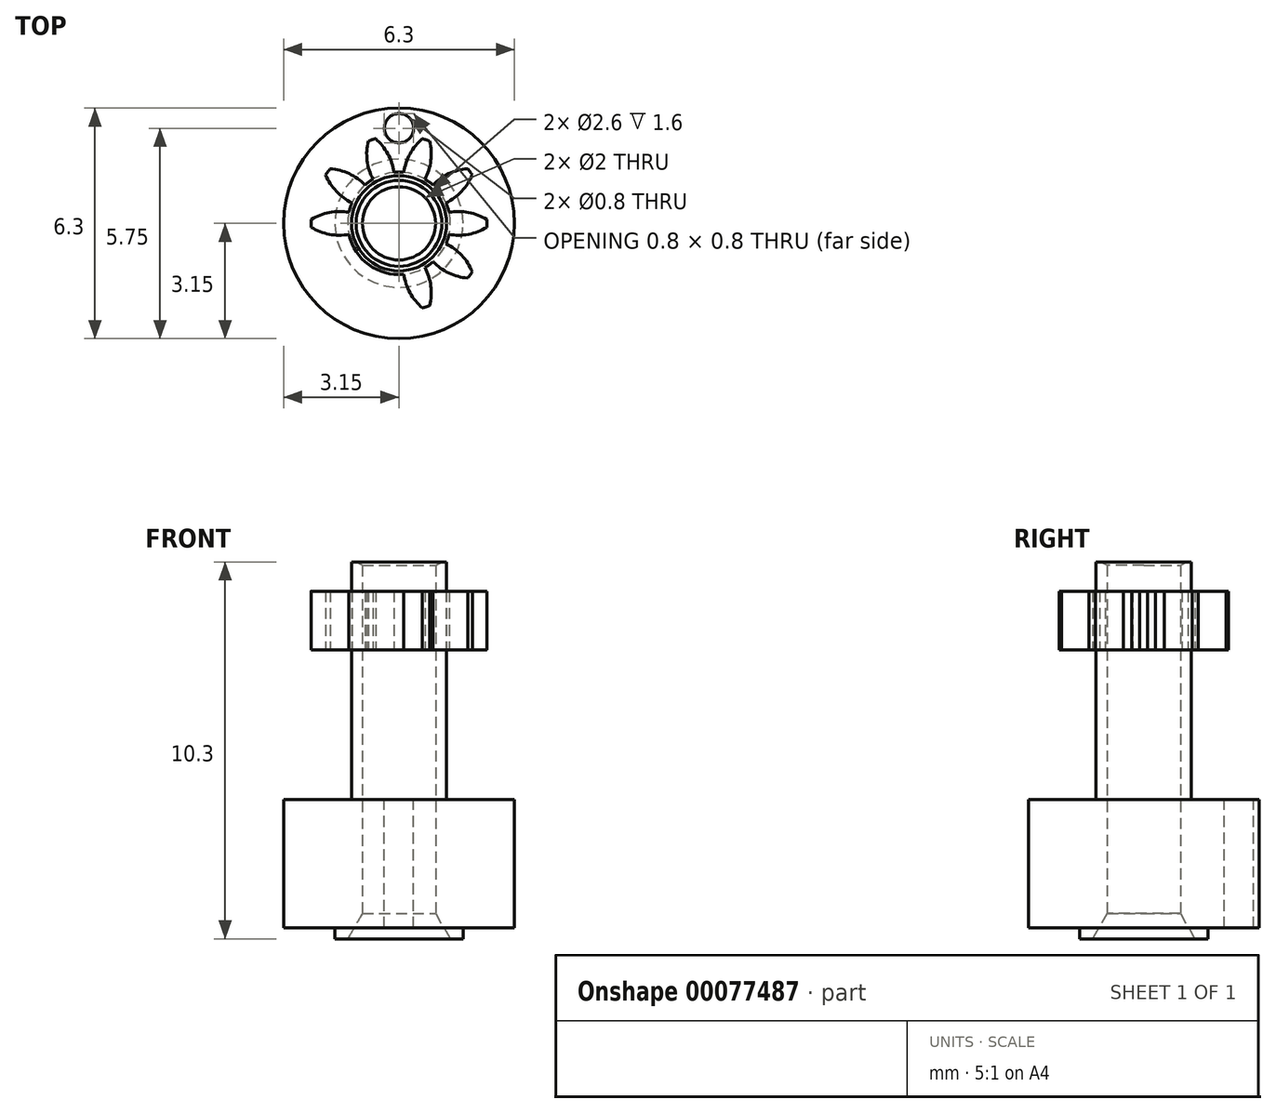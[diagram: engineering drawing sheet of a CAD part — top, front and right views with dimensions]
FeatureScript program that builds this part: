
annotation { "Feature Type Name" : "Feature", "Feature Type Description" : "" }
export const myFeature = defineFeature(function(context is Context, id is Id, definition is map)
    precondition{}
    {
        {
            var Q0;
            Q0=qCreatedBy(makeId("Front.planeOp"),FACE);
            var sketch = newSketch(context, id + "F0", { "sketchPlane" : qUnion([Q0])});
            skLineSegment(sketch, "E0", {"start": v(1.4, 0) * mm, "end": v(1.75, 0) * mm});
            skLineSegment(sketch, "E1", {"start": v(1.75, 0) * mm, "end": v(1.75, 0.3) * mm});
            skLineSegment(sketch, "E2", {"start": v(1.75, 0.3) * mm, "end": v(3.15, 0.3) * mm});
            skLineSegment(sketch, "E3", {"start": v(3.15, 0.3) * mm, "end": v(3.15, 3.8) * mm});
            skLineSegment(sketch, "E4", {"start": v(3.15, 3.8) * mm, "end": v(1.3, 3.8) * mm});
            skLineSegment(sketch, "E5", {"start": v(1.3, 3.8) * mm, "end": v(1.3, 10.3) * mm});
            skLineSegment(sketch, "E6", {"start": v(1.3, 10.3) * mm, "end": v(1, 10.3) * mm});
            skLineSegment(sketch, "E7", {"start": v(1, 10.3) * mm, "end": v(1, 0.7) * mm});
            skLineSegment(sketch, "E8", {"start": v(1, 0.7) * mm, "end": v(1.4, 0) * mm});
            skLineSegment(sketch, "E9", {"start": v(0, 0) * mm, "end": v(0, 10.3) * mm, "construction": true});
            skSolve(sketch);
        }
        {
            var Q0;
            Q0=makeQuery(id+"F0.imprint","IMPRINT",FACE,{"disambiguationData":[TD([[makeQuery(id+"F0.imprint","IMPRINT",EDGE,{"derivedFrom":sQuery(id+"F0.wireOp",EDGE,"E0")}),1.0]])]});
            var Q1;
            Q1=sQuery(id+"F0.wireOp",EDGE,"E9");
            revolve(context, id + "F1", {"entities" : qUnion([Q0]), "axis" : qUnion([Q1]), "revolveType" : RevolveType.FULL});
        }
        {
            var Q0;
            Q0=makeQuery(id+"F1.opRevolve","SWEPT_FACE",FACE,{"disambiguationData":[OSD([sQuery(id+"F0.wireOp",EDGE,"E6")])]});
            cPlane(context, id + "F2", {"entities" : qUnion([Q0]), "cplaneType" : CPlaneType.OFFSET, "offset" : 4.15 * mm, "oppositeDirection" : true, "width" : 150 * mm, "height" : 150 * mm});
        }
        {
            var Q0;
            Q0=qCreatedBy(id+"F2.planeOp",FACE);
            var sketch = newSketch(context, id + "F3", { "sketchPlane" : qUnion([Q0])});
            skCircle(sketch, "E10", {"center": v(0, 0) * mm, "radius": 2 * mm, "construction": true});
            skArc(sketch, "E11", {"start": v(-2.4, 0.1) * mm, "mid": v(-2.4, 0) * mm, "end": v(-2.4, -0.1) * mm});
            skCircle(sketch, "E12", {"center": v(0, 0) * mm, "radius": 1.4 * mm});
            skLineSegment(sketch, "E13", {"start": v(0, 0) * mm, "end": v(-1.94, -1.41) * mm, "construction": true});
            skArc(sketch, "E14", {"start": v(-1.37, 0.3) * mm, "mid": v(-1.9, 0.3) * mm, "end": v(-2.4, 0.1) * mm});
            skLineSegment(sketch, "E15", {"start": v(0, 0) * mm, "end": v(-1.94, 1.41) * mm, "construction": true});
            skArc(sketch, "E16", {"start": v(-2.4, -0.1) * mm, "mid": v(-1.9, -0.3) * mm, "end": v(-1.37, -0.3) * mm});
            skArc(sketch, "E17.1.0", {"start": v(-1.28, -0.56) * mm, "mid": v(-1.71, -0.88) * mm, "end": v(-2, -1.32) * mm});
            skArc(sketch, "E17.1.1", {"start": v(-1.88, -1.5) * mm, "mid": v(-1.36, -1.36) * mm, "end": v(-0.93, -1.05) * mm});
            skArc(sketch, "E17.1.2", {"start": v(-2, -1.32) * mm, "mid": v(-1.94, -1.41) * mm, "end": v(-1.88, -1.5) * mm});
            skArc(sketch, "E17.2.0", {"start": v(-0.71, -1.2) * mm, "mid": v(-0.87, -1.72) * mm, "end": v(-0.84, -2.25) * mm});
            skArc(sketch, "E17.2.1", {"start": v(-0.64, -2.31) * mm, "mid": v(-0.3, -1.9) * mm, "end": v(-0.13, -1.4) * mm});
            skArc(sketch, "E17.2.2", {"start": v(-0.84, -2.25) * mm, "mid": v(-0.74, -2.28) * mm, "end": v(-0.64, -2.31) * mm});
            skArc(sketch, "E17.3.0", {"start": v(0.13, -1.4) * mm, "mid": v(0.3, -1.9) * mm, "end": v(0.64, -2.31) * mm});
            skArc(sketch, "E17.3.1", {"start": v(0.84, -2.25) * mm, "mid": v(0.87, -1.72) * mm, "end": v(0.71, -1.2) * mm});
            skArc(sketch, "E17.3.2", {"start": v(0.64, -2.31) * mm, "mid": v(0.74, -2.28) * mm, "end": v(0.84, -2.25) * mm});
            skArc(sketch, "E17.4.0", {"start": v(0.93, -1.05) * mm, "mid": v(1.36, -1.36) * mm, "end": v(1.88, -1.5) * mm});
            skArc(sketch, "E17.4.1", {"start": v(2, -1.32) * mm, "mid": v(1.71, -0.88) * mm, "end": v(1.28, -0.56) * mm});
            skArc(sketch, "E17.4.2", {"start": v(1.88, -1.5) * mm, "mid": v(1.94, -1.41) * mm, "end": v(2, -1.32) * mm});
            skArc(sketch, "E17.5.0", {"start": v(1.37, -0.3) * mm, "mid": v(1.9, -0.3) * mm, "end": v(2.4, -0.1) * mm});
            skArc(sketch, "E17.5.1", {"start": v(2.4, 0.1) * mm, "mid": v(1.9, 0.3) * mm, "end": v(1.37, 0.3) * mm});
            skArc(sketch, "E17.5.2", {"start": v(2.4, -0.1) * mm, "mid": v(2.4, 0) * mm, "end": v(2.4, 0.1) * mm});
            skArc(sketch, "E17.6.0", {"start": v(1.28, 0.56) * mm, "mid": v(1.71, 0.88) * mm, "end": v(2, 1.32) * mm});
            skArc(sketch, "E17.6.1", {"start": v(1.88, 1.5) * mm, "mid": v(1.36, 1.36) * mm, "end": v(0.93, 1.05) * mm});
            skArc(sketch, "E17.6.2", {"start": v(2, 1.32) * mm, "mid": v(1.94, 1.41) * mm, "end": v(1.88, 1.5) * mm});
            skArc(sketch, "E17.7.0", {"start": v(0.71, 1.2) * mm, "mid": v(0.87, 1.72) * mm, "end": v(0.84, 2.25) * mm});
            skArc(sketch, "E17.7.1", {"start": v(0.64, 2.31) * mm, "mid": v(0.3, 1.9) * mm, "end": v(0.13, 1.4) * mm});
            skArc(sketch, "E17.7.2", {"start": v(0.84, 2.25) * mm, "mid": v(0.74, 2.28) * mm, "end": v(0.64, 2.31) * mm});
            skArc(sketch, "E17.8.0", {"start": v(-0.13, 1.4) * mm, "mid": v(-0.3, 1.9) * mm, "end": v(-0.64, 2.31) * mm});
            skArc(sketch, "E17.8.1", {"start": v(-0.84, 2.25) * mm, "mid": v(-0.87, 1.72) * mm, "end": v(-0.71, 1.2) * mm});
            skArc(sketch, "E17.8.2", {"start": v(-0.64, 2.31) * mm, "mid": v(-0.74, 2.28) * mm, "end": v(-0.84, 2.25) * mm});
            skArc(sketch, "E17.9.0", {"start": v(-0.93, 1.05) * mm, "mid": v(-1.36, 1.36) * mm, "end": v(-1.88, 1.5) * mm});
            skArc(sketch, "E17.9.1", {"start": v(-2, 1.32) * mm, "mid": v(-1.71, 0.88) * mm, "end": v(-1.28, 0.56) * mm});
            skArc(sketch, "E17.9.2", {"start": v(-1.88, 1.5) * mm, "mid": v(-1.94, 1.41) * mm, "end": v(-2, 1.32) * mm});
            skCircle(sketch, "E18", {"center": v(0, 0) * mm, "radius": 1.3 * mm});
            skSolve(sketch);
        }
        {
            var Q0;
            {var subQ6=sQuery(id+"F3.wireOp",EDGE,"E17.6.0");var subQ12=sQuery(id+"F3.wireOp",EDGE,"E17.7.0");var subQ17=sQuery(id+"F3.wireOp",EDGE,"E17.8.0");var subQ21=sQuery(id+"F3.wireOp",EDGE,"E17.9.0");var subQ27=sQuery(id+"F3.wireOp",EDGE,"E17.1.0");var subQ32=sQuery(id+"F3.wireOp",EDGE,"E17.2.0");var subQ37=sQuery(id+"F3.wireOp",EDGE,"E17.3.0");var subQ42=sQuery(id+"F3.wireOp",EDGE,"E17.4.0");var subQ47=sQuery(id+"F3.wireOp",EDGE,"E17.5.0");Q0=qUnion([makeQuery(id+"F3.imprint","IMPRINT",FACE,{"disambiguationData":[TD([[makeQuery(id+"F3.imprint","IMPRINT",EDGE,{"derivedFrom":sQuery(id+"F3.wireOp",EDGE,"E11")}),1.0]])]}),makeQuery(id+"F3.imprint","IMPRINT",FACE,{"disambiguationData":[TD([[makeQuery(id+"F3.imprint","IMPRINT",EDGE,{"derivedFrom":subQ6}),1.0]])]}),makeQuery(id+"F3.imprint","IMPRINT",FACE,{"disambiguationData":[TD([[makeQuery(id+"F3.imprint","IMPRINT",EDGE,{"derivedFrom":subQ12}),1.0]])]}),makeQuery(id+"F3.imprint","IMPRINT",FACE,{"disambiguationData":[TD([[makeQuery(id+"F3.imprint","IMPRINT",EDGE,{"derivedFrom":subQ17}),1.0]])]}),makeQuery(id+"F3.imprint","IMPRINT",FACE,{"disambiguationData":[TD([[makeQuery(id+"F3.imprint","IMPRINT",EDGE,{"derivedFrom":subQ21}),1.0]])]}),makeQuery(id+"F3.imprint","IMPRINT",FACE,{"disambiguationData":[TD([[makeQuery(id+"F3.imprint","IMPRINT",EDGE,{"derivedFrom":subQ27}),1.0]])]}),makeQuery(id+"F3.imprint","IMPRINT",FACE,{"disambiguationData":[TD([[makeQuery(id+"F3.imprint","IMPRINT",EDGE,{"derivedFrom":subQ32}),1.0]])]}),makeQuery(id+"F3.imprint","IMPRINT",FACE,{"disambiguationData":[TD([[makeQuery(id+"F3.imprint","IMPRINT",EDGE,{"derivedFrom":subQ37}),1.0]])]}),makeQuery(id+"F3.imprint","IMPRINT",FACE,{"disambiguationData":[TD([[makeQuery(id+"F3.imprint","IMPRINT",EDGE,{"derivedFrom":subQ42}),1.0]])]}),makeQuery(id+"F3.imprint","IMPRINT",FACE,{"disambiguationData":[TD([[makeQuery(id+"F3.imprint","IMPRINT",EDGE,{"derivedFrom":subQ47}),1.0]])]}),makeQuery(id+"F3.imprint","IMPRINT",FACE,{"disambiguationData":[TD([[makeQuery(id+"F3.imprint","IMPRINT",EDGE,{"derivedFrom":sQuery(id+"F3.wireOp",EDGE,"E18")}),-1.0]])]})]);}
            extrude(context, id + "F4", {"entities" : qUnion([Q0]), "depth" : 3.35 * mm});
        }
        {
            var Q0;
            Q0=makeQuery(id+"F1.opRevolve","SWEPT_FACE",FACE,{"disambiguationData":[OSD([sQuery(id+"F0.wireOp",EDGE,"E4")])]});
            var sketch = newSketch(context, id + "F5", { "sketchPlane" : qUnion([Q0])});
            skCircle(sketch, "E19", {"center": v(0, 2.6) * mm, "radius": 0.4 * mm});
            skSolve(sketch);
        }
        {
            var Q0;
            Q0=makeQuery(id+"F5.imprint","IMPRINT",FACE,{"disambiguationData":[TD([[makeQuery(id+"F5.imprint","IMPRINT",EDGE,{"derivedFrom":sQuery(id+"F5.wireOp",EDGE,"E19")}),1.0]])]});
            extrude(context, id + "F6", {"entities" : qUnion([Q0]), "operationType" : NewBodyOperationType.REMOVE, "endBound" : BoundingType.THROUGH_ALL, "oppositeDirection" : true, "depth" : 25 * mm});
        }
        {
            var Q0;
            Q0=makeQuery(id+"F1.opRevolve","SWEPT_BODY",BODY,{"disambiguationData":[OSD([sQuery(id+"F0.wireOp",EDGE,"E0"),sQuery(id+"F0.wireOp",EDGE,"E1"),sQuery(id+"F0.wireOp",EDGE,"E2"),sQuery(id+"F0.wireOp",EDGE,"E3"),sQuery(id+"F0.wireOp",EDGE,"E4"),sQuery(id+"F0.wireOp",EDGE,"E5"),sQuery(id+"F0.wireOp",EDGE,"E6"),sQuery(id+"F0.wireOp",EDGE,"E7"),sQuery(id+"F0.wireOp",EDGE,"E8")])]});
            var Q1;
            Q1=makeQuery(id+"F4.opExtrude","SWEPT_BODY",BODY,{"disambiguationData":[OSD([sQuery(id+"F3.wireOp",EDGE,"E11"),sQuery(id+"F3.wireOp",EDGE,"E12"),sQuery(id+"F3.wireOp",EDGE,"E14"),sQuery(id+"F3.wireOp",EDGE,"E16"),sQuery(id+"F3.wireOp",EDGE,"E17.1.0"),sQuery(id+"F3.wireOp",EDGE,"E17.1.1"),sQuery(id+"F3.wireOp",EDGE,"E17.1.2"),sQuery(id+"F3.wireOp",EDGE,"E17.2.0"),sQuery(id+"F3.wireOp",EDGE,"E17.2.1"),sQuery(id+"F3.wireOp",EDGE,"E17.2.2"),sQuery(id+"F3.wireOp",EDGE,"E17.3.0"),sQuery(id+"F3.wireOp",EDGE,"E17.3.1"),sQuery(id+"F3.wireOp",EDGE,"E17.3.2"),sQuery(id+"F3.wireOp",EDGE,"E17.4.0"),sQuery(id+"F3.wireOp",EDGE,"E17.4.1"),sQuery(id+"F3.wireOp",EDGE,"E17.4.2"),sQuery(id+"F3.wireOp",EDGE,"E17.5.0"),sQuery(id+"F3.wireOp",EDGE,"E17.5.1"),sQuery(id+"F3.wireOp",EDGE,"E17.5.2"),sQuery(id+"F3.wireOp",EDGE,"E17.6.0"),sQuery(id+"F3.wireOp",EDGE,"E17.6.1"),sQuery(id+"F3.wireOp",EDGE,"E17.6.2"),sQuery(id+"F3.wireOp",EDGE,"E17.7.0"),sQuery(id+"F3.wireOp",EDGE,"E17.7.1"),sQuery(id+"F3.wireOp",EDGE,"E17.7.2"),sQuery(id+"F3.wireOp",EDGE,"E17.8.0"),sQuery(id+"F3.wireOp",EDGE,"E17.8.1"),sQuery(id+"F3.wireOp",EDGE,"E17.8.2"),sQuery(id+"F3.wireOp",EDGE,"E17.9.0"),sQuery(id+"F3.wireOp",EDGE,"E17.9.1"),sQuery(id+"F3.wireOp",EDGE,"E17.9.2"),sQuery(id+"F3.wireOp",EDGE,"E18")])]});
            transform(context, id + "F7", {"entities" : qUnion([Q0, Q1]), "transformType" : TransformType.COPY});
        }
        {
            var Q0;
            Q0=makeQuery(id+"F7.opPattern","COPY",BODY,{"derivedFrom":makeQuery(id+"F1.opRevolve","SWEPT_BODY",BODY,{"disambiguationData":[OSD([sQuery(id+"F0.wireOp",EDGE,"E0"),sQuery(id+"F0.wireOp",EDGE,"E1"),sQuery(id+"F0.wireOp",EDGE,"E2"),sQuery(id+"F0.wireOp",EDGE,"E3"),sQuery(id+"F0.wireOp",EDGE,"E4"),sQuery(id+"F0.wireOp",EDGE,"E5"),sQuery(id+"F0.wireOp",EDGE,"E6"),sQuery(id+"F0.wireOp",EDGE,"E7"),sQuery(id+"F0.wireOp",EDGE,"E8")])]}),"instanceName":"1"});
            deleteBodies(context, id + "F8", {"entities" : qUnion([Q0])});
        }
        {
            var Q0;
            Q0=makeQuery(id+"F1.opRevolve","SWEPT_EDGE",EDGE,{"disambiguationData":[OSD([sQuery(id+"F0.wireOp",EDGE,"E6"),sQuery(id+"F0.wireOp",EDGE,"E7")])]});
            chamfer(context, id + "F9", {"entities" : qUnion([Q0]), "chamferType" : ChamferType.OFFSET_ANGLE, "width" : 0.1 * mm, "oppositeDirection" : true, "angle" : 60 * degree, "tangentPropagation" : true});
        }
        {
            var Q0;
            Q0=qCreatedBy(makeId("Front.planeOp"),FACE);
            var sketch = newSketch(context, id + "F10", { "sketchPlane" : qUnion([Q0])});
            skLineSegment(sketch, "E20", {"start": v(0, 0) * mm, "end": v(0, 10.3) * mm, "construction": true});
            skLineSegment(sketch, "E21.bottom", {"start": v(1.3, 7.9) * mm, "end": v(2.4, 7.9) * mm});
            skLineSegment(sketch, "E21.top", {"start": v(1.3, 6.8) * mm, "end": v(2.4, 6.8) * mm});
            skLineSegment(sketch, "E21.left", {"start": v(1.3, 7.9) * mm, "end": v(1.3, 6.8) * mm});
            skLineSegment(sketch, "E21.right", {"start": v(2.4, 7.9) * mm, "end": v(2.4, 6.8) * mm});
            skSolve(sketch);
        }
        {
            var Q0;
            Q0=makeQuery(id+"F10.imprint","IMPRINT",FACE,{"disambiguationData":[TD([[makeQuery(id+"F10.imprint","IMPRINT",EDGE,{"derivedFrom":sQuery(id+"F10.wireOp",EDGE,"E21.bottom")}),-1.0]])]});
            var Q1;
            Q1=sQuery(id+"F10.wireOp",EDGE,"E20");
            revolve(context, id + "F11", {"operationType" : NewBodyOperationType.REMOVE, "entities" : qUnion([Q0]), "axis" : qUnion([Q1]), "revolveType" : RevolveType.FULL, "oppositeDirection" : true});
        }
        {
            var Q0;
            {var subQ1=sQuery(id+"F3.wireOp",EDGE,"E17.2.0");Q0=makeQuery(id+"F3.imprint","IMPRINT",FACE,{"disambiguationData":[TD([[makeQuery(id+"F3.imprint","IMPRINT",EDGE,{"derivedFrom":subQ1}),1.0]])]});}
            var Q1;
            {var subQ1=sQuery(id+"F3.wireOp",EDGE,"E17.1.0");Q1=makeQuery(id+"F3.imprint","IMPRINT",FACE,{"disambiguationData":[TD([[makeQuery(id+"F3.imprint","IMPRINT",EDGE,{"derivedFrom":subQ1}),1.0]])]});}
            extrude(context, id + "F12", {"entities" : qUnion([Q0, Q1]), "operationType" : NewBodyOperationType.REMOVE, "depth" : 25 * mm});
        }
        {
            var Q0;
            Q0=makeQuery(id+"F1.opRevolve","SWEPT_BODY",BODY,{"disambiguationData":[OSD([sQuery(id+"F0.wireOp",EDGE,"E0"),sQuery(id+"F0.wireOp",EDGE,"E1"),sQuery(id+"F0.wireOp",EDGE,"E2"),sQuery(id+"F0.wireOp",EDGE,"E3"),sQuery(id+"F0.wireOp",EDGE,"E4"),sQuery(id+"F0.wireOp",EDGE,"E5"),sQuery(id+"F0.wireOp",EDGE,"E6"),sQuery(id+"F0.wireOp",EDGE,"E7"),sQuery(id+"F0.wireOp",EDGE,"E8")])]});
            transform(context, id + "F13", {"entities" : qUnion([Q0]), "transformType" : TransformType.TRANSLATION_3D, "dx" : 0 * mm, "dy" : 0 * mm, "dz" : 0 * mm, "makeCopy" : true});
        }
        {
            var Q0;
            Q0=makeQuery(id+"F7.opPattern","COPY",FACE,{"derivedFrom":makeQuery(id+"F4.opExtrude","CAP_FACE",FACE,{"disambiguationData":[OSD([sQuery(id+"F3.wireOp",EDGE,"E11"),sQuery(id+"F3.wireOp",EDGE,"E12"),sQuery(id+"F3.wireOp",EDGE,"E14"),sQuery(id+"F3.wireOp",EDGE,"E16"),sQuery(id+"F3.wireOp",EDGE,"E17.1.0"),sQuery(id+"F3.wireOp",EDGE,"E17.1.1"),sQuery(id+"F3.wireOp",EDGE,"E17.1.2"),sQuery(id+"F3.wireOp",EDGE,"E17.2.0"),sQuery(id+"F3.wireOp",EDGE,"E17.2.1"),sQuery(id+"F3.wireOp",EDGE,"E17.2.2"),sQuery(id+"F3.wireOp",EDGE,"E17.3.0"),sQuery(id+"F3.wireOp",EDGE,"E17.3.1"),sQuery(id+"F3.wireOp",EDGE,"E17.3.2"),sQuery(id+"F3.wireOp",EDGE,"E17.4.0"),sQuery(id+"F3.wireOp",EDGE,"E17.4.1"),sQuery(id+"F3.wireOp",EDGE,"E17.4.2"),sQuery(id+"F3.wireOp",EDGE,"E17.5.0"),sQuery(id+"F3.wireOp",EDGE,"E17.5.1"),sQuery(id+"F3.wireOp",EDGE,"E17.5.2"),sQuery(id+"F3.wireOp",EDGE,"E17.6.0"),sQuery(id+"F3.wireOp",EDGE,"E17.6.1"),sQuery(id+"F3.wireOp",EDGE,"E17.6.2"),sQuery(id+"F3.wireOp",EDGE,"E17.7.0"),sQuery(id+"F3.wireOp",EDGE,"E17.7.1"),sQuery(id+"F3.wireOp",EDGE,"E17.7.2"),sQuery(id+"F3.wireOp",EDGE,"E17.8.0"),sQuery(id+"F3.wireOp",EDGE,"E17.8.1"),sQuery(id+"F3.wireOp",EDGE,"E17.8.2"),sQuery(id+"F3.wireOp",EDGE,"E17.9.0"),sQuery(id+"F3.wireOp",EDGE,"E17.9.1"),sQuery(id+"F3.wireOp",EDGE,"E17.9.2"),sQuery(id+"F3.wireOp",EDGE,"E18")])],"isStart":true}),"instanceName":"1"});
            extrude(context, id + "F14", {"entities" : qUnion([Q0]), "operationType" : NewBodyOperationType.REMOVE, "oppositeDirection" : true, "depth" : 0.85 * mm});
        }
        {
            var Q0;
            {var subQ1=sQuery(id+"F3.wireOp",EDGE,"E17.2.0");Q0=makeQuery(id+"F3.imprint","IMPRINT",FACE,{"disambiguationData":[TD([[makeQuery(id+"F3.imprint","IMPRINT",EDGE,{"derivedFrom":subQ1}),1.0]])]});}
            var Q1;
            {var subQ1=sQuery(id+"F3.wireOp",EDGE,"E17.1.0");Q1=makeQuery(id+"F3.imprint","IMPRINT",FACE,{"disambiguationData":[TD([[makeQuery(id+"F3.imprint","IMPRINT",EDGE,{"derivedFrom":subQ1}),1.0]])]});}
            extrude(context, id + "F15", {"entities" : qUnion([Q0, Q1]), "operationType" : NewBodyOperationType.REMOVE, "depth" : 1.75 * mm});
        }
    });
